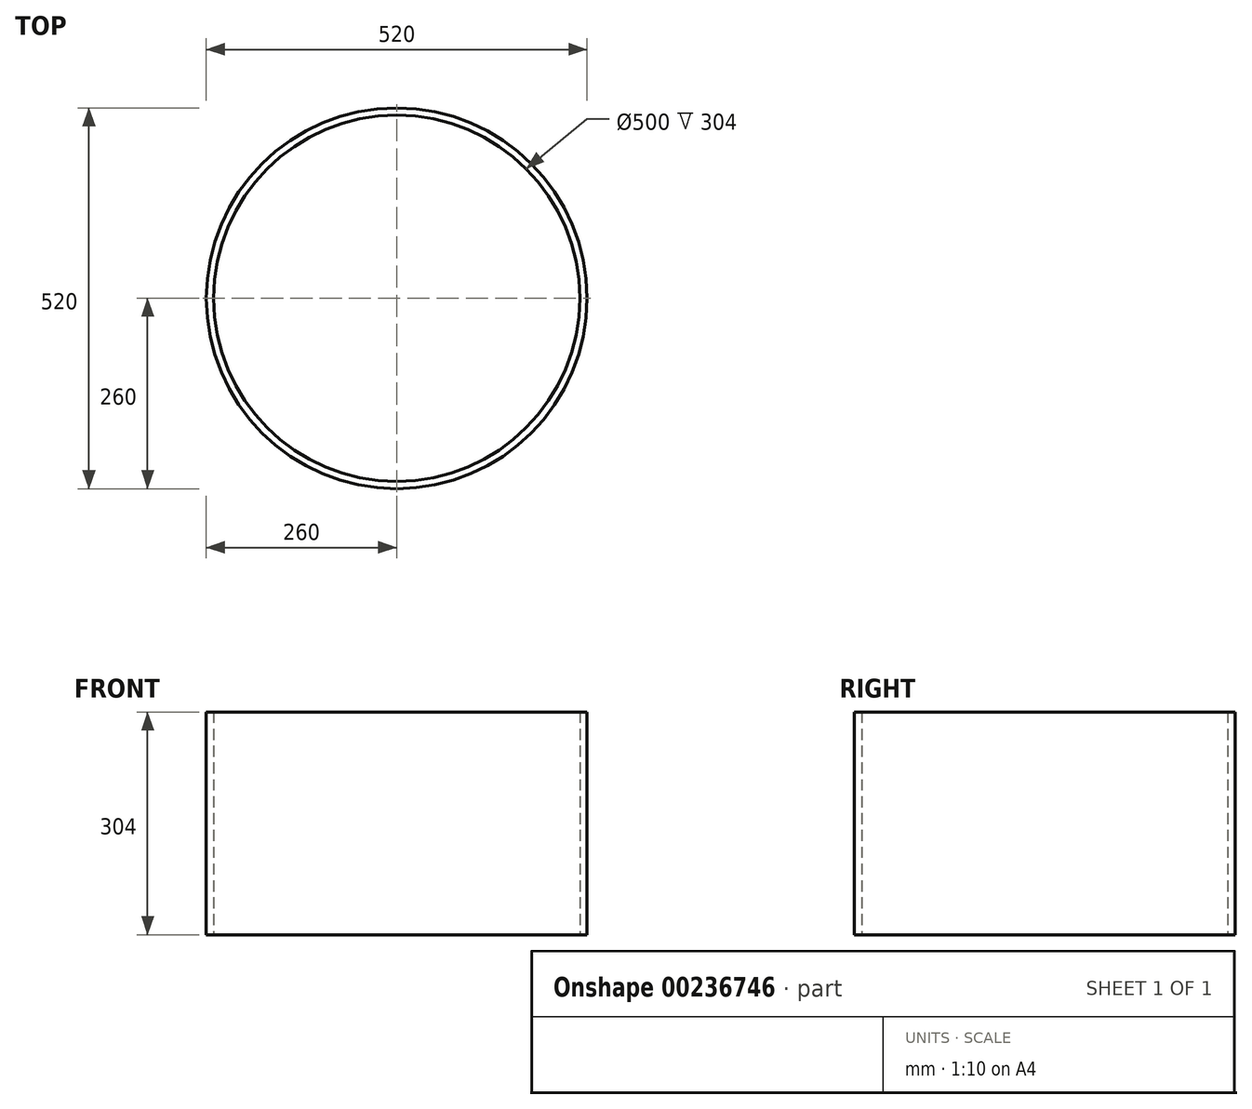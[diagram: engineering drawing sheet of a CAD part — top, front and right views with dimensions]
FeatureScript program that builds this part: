
annotation { "Feature Type Name" : "Feature", "Feature Type Description" : "" }
export const myFeature = defineFeature(function(context is Context, id is Id, definition is map)
    precondition{}
    {
        {
            var Q0;
            Q0=qCreatedBy(makeId("Top.planeOp"),FACE);
            var sketch = newSketch(context, id + "F0", { "sketchPlane" : qUnion([Q0])});
            skCircle(sketch, "E0", {"center": v(0, 0) * mm, "radius": 260 * mm});
            skCircle(sketch, "E1", {"center": v(0, 0) * mm, "radius": 250 * mm});
            skSolve(sketch);
        }
        {
            var Q0;
            Q0 = qSketchRegion(id + "F0", true);
            extrude(context, id + "F1", {"entities" : qUnion([Q0]), "depth" : 304 * mm, "offsetDistance" : 25 * mm});
        }
    });
